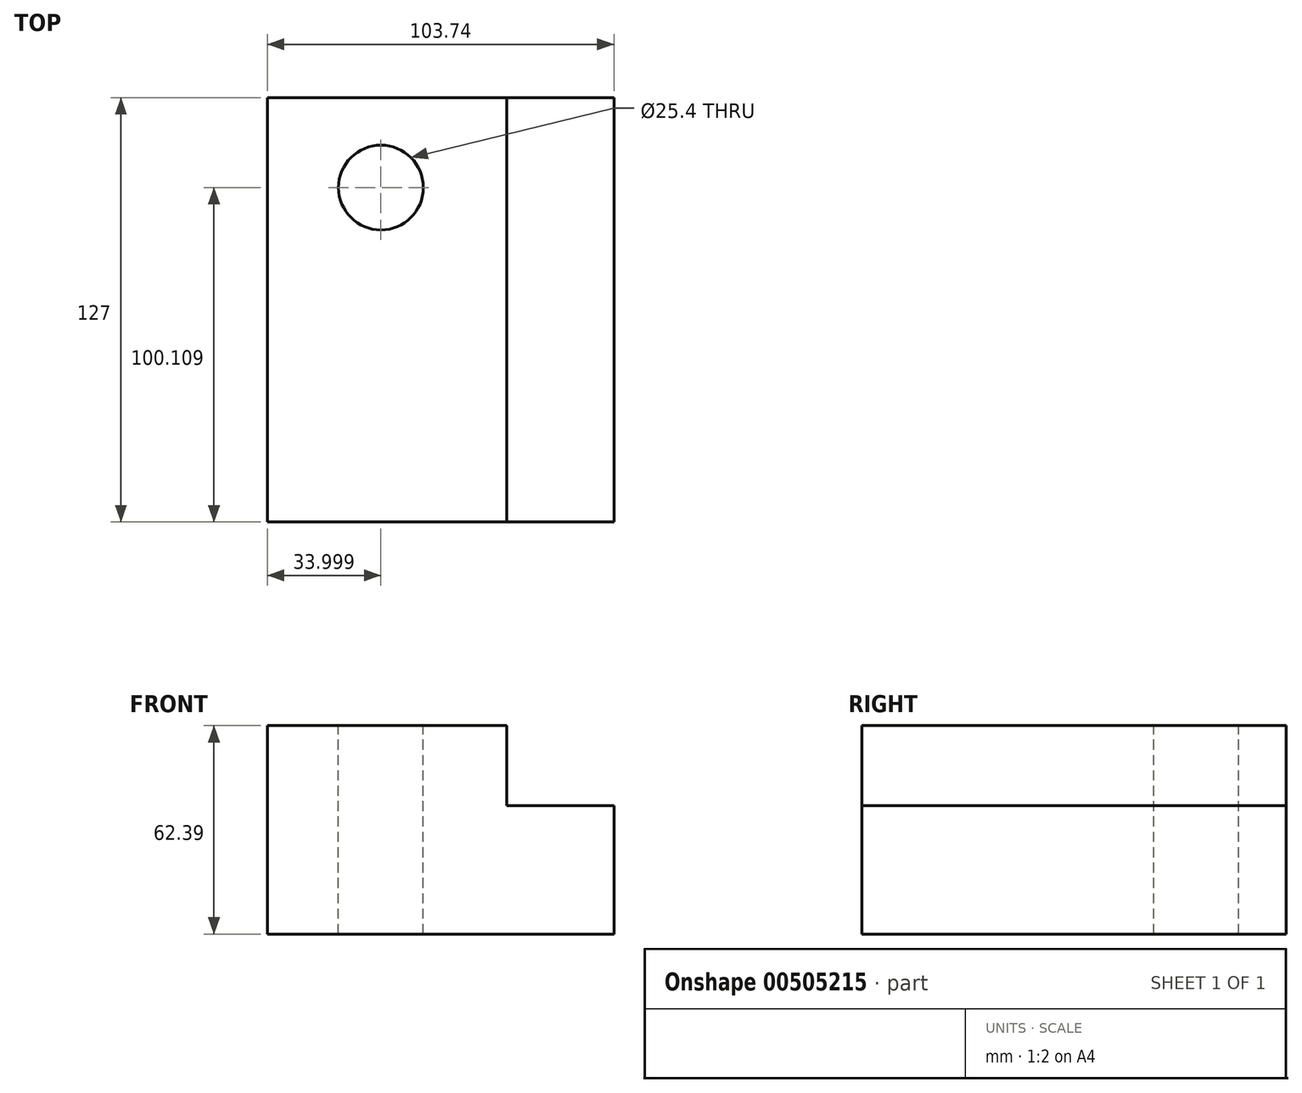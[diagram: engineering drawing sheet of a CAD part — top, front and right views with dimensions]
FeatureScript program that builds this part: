
annotation { "Feature Type Name" : "Feature", "Feature Type Description" : "" }
export const myFeature = defineFeature(function(context is Context, id is Id, definition is map)
    precondition{}
    {
        {
            var Q0;
            Q0=qCreatedBy(makeId("Front.planeOp"),FACE);
            var sketch = newSketch(context, id + "F0", { "sketchPlane" : qUnion([Q0])});
            skLineSegment(sketch, "E0.bottom", {"start": v(0, 0) * mm, "end": v(103.74, 0) * mm});
            skLineSegment(sketch, "E0.top", {"start": v(0, 62.4) * mm, "end": v(103.74, 62.4) * mm});
            skLineSegment(sketch, "E0.left", {"start": v(0, 0) * mm, "end": v(0, 62.4) * mm});
            skLineSegment(sketch, "E0.right", {"start": v(103.74, 0) * mm, "end": v(103.74, 62.4) * mm});
            skLineSegment(sketch, "E1.bottom", {"start": v(103.74, 62.4) * mm, "end": v(71.7, 62.4) * mm});
            skLineSegment(sketch, "E1.top", {"start": v(103.74, 38.41) * mm, "end": v(71.7, 38.41) * mm});
            skLineSegment(sketch, "E1.left", {"start": v(103.74, 62.4) * mm, "end": v(103.74, 38.41) * mm});
            skLineSegment(sketch, "E1.right", {"start": v(71.7, 62.4) * mm, "end": v(71.7, 38.41) * mm});
            skSolve(sketch);
        }
        {
            var Q0;
            Q0=makeQuery(id+"F0.imprint","IMPRINT",FACE,{"disambiguationData":[TD([[makeQuery(id+"F0.imprint","IMPRINT",EDGE,{"derivedFrom":sQuery(id+"F0.wireOp",EDGE,"E0.bottom")}),1.0]])]});
            extrude(context, id + "F1", {"entities" : qUnion([Q0]), "oppositeDirection" : true, "depth" : 127 * mm});
        }
        {
            var Q0;
            Q0=makeQuery(id+"F1.opExtrude","SWEPT_FACE",FACE,{"disambiguationData":[OSD([sQuery(id+"F0.wireOp",EDGE,"E0.top")])]});
            var sketch = newSketch(context, id + "F2", { "sketchPlane" : qUnion([Q0])});
            skCircle(sketch, "E2", {"center": v(34, 100.1) * mm, "radius": 12.7 * mm});
            skSolve(sketch);
        }
        {
            var Q0;
            Q0 = qSketchRegion(id + "F2", true);
            var Q1;
            Q1=makeQuery(id+"F1.opExtrude","SWEPT_FACE",FACE,{"disambiguationData":[OSD([sQuery(id+"F0.wireOp",EDGE,"E0.bottom")])]});
            extrude(context, id + "F3", {"entities" : qUnion([Q0]), "operationType" : NewBodyOperationType.REMOVE, "endBound" : BoundingType.UP_TO_SURFACE, "oppositeDirection" : true, "endBoundEntityFace" : qUnion([Q1]), "depth" : 25.4 * mm});
        }
    });
